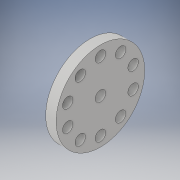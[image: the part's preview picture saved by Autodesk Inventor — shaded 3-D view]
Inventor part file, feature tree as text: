
AUTODESK INVENTOR PART (.ipt)
format: ipt  version: 2017 (Build 210142000, 142)  size: 138,240 bytes
history: native  units: in
note: dims shown in document units (in); Inventor stores cm internally (conversion verified against a paired STEP export)
features: sketch x3, hole x2, revolve x1
ambient origin geometry x8: Origin, YZ Plane, XZ Plane, XY Plane, X Axis, Y Axis, Z Axis, Center Point
bodies: Solid1 (feature_tree)
feature tree (6):
  revolve  "Revolution1"  [1 undecoded]
  hole  "Hole1"  [1 undecoded]
  hole  "Hole2"  [1 undecoded]
  sketch  "Sketch1"  dims[d0=0.625in d1=0.5in]
  sketch  "Sketch2"  dims[d2=1.5in d3=0.5in]
  sketch  "Sketch3"  dims[d4=90.0deg d5=0.5in d6=0.75in d7=0.375in d8=0.25in d9=0.5635in d10=1.0in d11=0.8108in d13=3.3in d14=3.937in d16=360.0deg d18=0.5in d19=0.75in d20=0.375in d21=0.25in d22=0.5635in d23=1.0in d24=0.8108in]
note: 3 required parameter values undecoded (feature->parameter linkage not recoverable at this tier; creation-order binding heuristic only, values carry confidence <= 0.55)